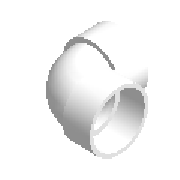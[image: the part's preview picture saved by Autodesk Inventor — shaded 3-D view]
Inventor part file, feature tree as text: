
AUTODESK INVENTOR PART (.ipt)
format: ipt  version: 2023.2 (Build 272271030, 271C)  size: 240,128 bytes
history: native  units: mm (DEFAULTED — no unit token found)
features: other x6, sketch x4
ambient origin geometry x8: Origin, YZ Plane, XZ Plane, XY Plane, X Axis, Y Axis, Z Axis, Center Point
bodies: Solid1 (feature_tree)
feature tree (10):
  other  "Work Point1"
  other  "Work Point2"
  other  "Work Axis1"
  other  "Work Point3"
  other  "Work Axis2"
  other  "Work Point4"
  sketch  "Sketch1"  dims[d1=48.3mm]
  sketch  "Sketch2"  dims[d2=47.8mm]
  sketch  "Sketch3"  dims[d0=48.3mm]
  sketch  "Sketch4"  dims[d3=47.8mm d4=2.5mm d5=22.0mm d6=2.5mm d7=40.0mm d39=90.0deg d8=40.0mm d9=2.7mm d10=24.5mm d11=24.5mm d12=24.5mm d13=0.0mm d14=2.7mm d15=22.0mm d16=2.5mm d17=48.3mm d18=47.8mm d19=40.0mm d82=90.0deg d83=0.0mm]
